# Revit family: Electronics_Desono_Biamp_Two-Way-High-Efficiency-Loudspeaker_DX-IC4LP
name_source: partatom
category: Communication Devices
units: mm (PartAtom-declared; Revit-internal decimal feet)

## family parameters
Cut with Voids When Loaded = No
Host = Face
Maintain Annotation Orientation = No
OmniClass Number = 23.85.10.11.14.14.14
OmniClass Title = Loudspeakers
Part Type = Normal
Room Calculation Point = No
Round Connector Dimension = Use Diameter
Shared = No

## types (1)
- DX-IC4LP
    Autoformer = 70 V: 30 W, 15 W, 7.5 W, 3.75 W; 100 V: 30 W, 15 W, 7.5 W
    Certifcations = ETL listed to comply with UL1480A, UL2043 and CSA62368-1 Suitable for use in air handling spaces per NFPA 70 and NFPA 90
    Connector Description = 4-way Euroblock; Low impedance 8 ohms, 70/100V operation
    Controls = Front-face wattage / low impedance selector switch
    Crossover Frequency = 2 kHz
    Default Elevation = 4' - 0"
    Depth = 0' - 4"
    Description = Desono™ DX-IC4LP Two-Way 4.5 Low Profile High Efficiency Ceiling Mount Loudspeaker
    Diameter = 0' - 10"
    Grill Material = Biamp - Plastic - White(Grid)
    Housing Material = Biamp - Plastic - Black
    Input Connection = 4-position Euroblock connector
    Manufacturer = Biamp
    Model = DX-IC4LP
    Mounting Provisions = 2 SpringLock mounting clamps with 1.3-inch grip range
    Nominal Beamwidth (H x V) = 165°, conical
    Nominal Continuous Power = Passive - 22 V; (60 W @ 8 Ω)
    Nominal Maximum SPL = Passive: Peak - 114dB; Continuous - 108dB
    Operating Environment = Indoor
    Operating Mode = Passive with DSP
    Operating Range (-10dB) = 115 Hz to 20 kHz
    Product Documentation Link = https://downloads.biamp.com
    Product Page URL = https://www.biamp.com
    Product data url = https://www.bimobject.com
    Rated Continuous Voltage = Passive: 17.8 V; (25 dBV)
    Rated Maximum SPL (Processed) = Passive: Peak - 118dB; Continuous - 106dB
    Recommended Amplifers = Passive: 60 W - 120 W into 8 Ω, (22 V - 31 V)
    Required Accessory = 135 Hz, 12 dB/oct. high pass flter
    Sensitivity = 91 dB (2.83 V); 91 dB (1 W at rated impedance 8 Ω)
    Shipping Weight = 20.28 lb
    Transducers = LF 1 x 4.5 (114 mm); HF 1 x 0.75 (19 mm) exit compression driver
    URL = https://www.biamp.com
    Weight = 5.86 lb

## geometry (parser evidence)
native form markers: Sweep x8
no freeform markers — native parametric forms only
